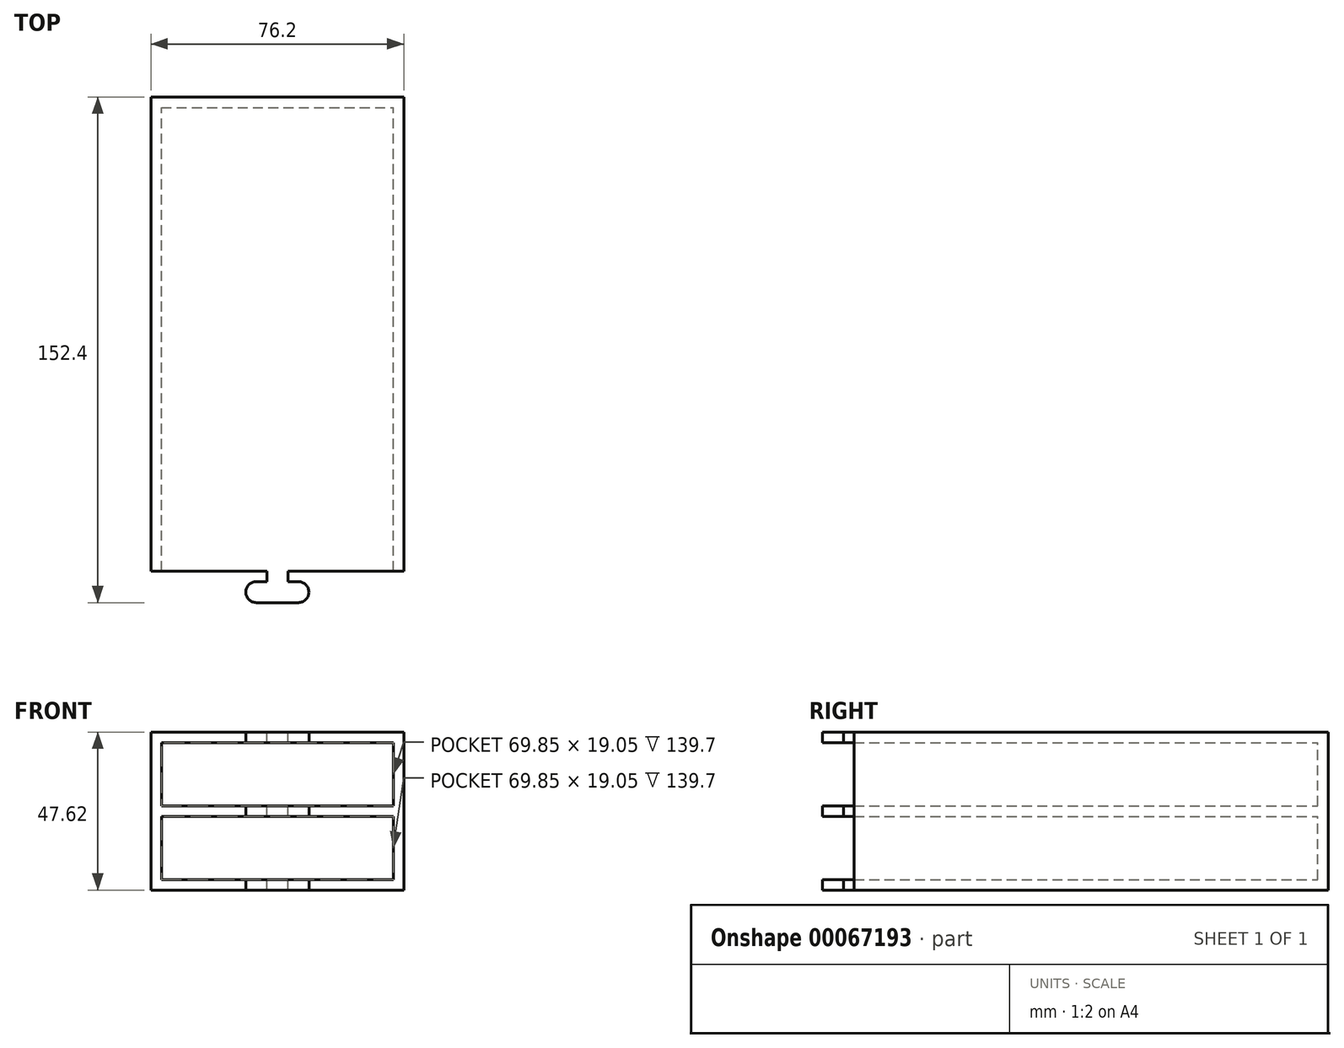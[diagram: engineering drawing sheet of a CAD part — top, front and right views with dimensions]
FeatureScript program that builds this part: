
annotation { "Feature Type Name" : "Feature", "Feature Type Description" : "" }
export const myFeature = defineFeature(function(context is Context, id is Id, definition is map)
    precondition{}
    {
        {
            var Q0;
            Q0=qCreatedBy(makeId("Front.planeOp"),FACE);
            var sketch = newSketch(context, id + "F0", { "sketchPlane" : qUnion([Q0])});
            skLineSegment(sketch, "E0.bottom", {"start": v(0, 0) * mm, "end": v(76.2, 0) * mm});
            skLineSegment(sketch, "E0.top", {"start": v(0, 47.63) * mm, "end": v(76.2, 47.63) * mm});
            skLineSegment(sketch, "E0.left", {"start": v(0, 0) * mm, "end": v(0, 47.63) * mm});
            skLineSegment(sketch, "E0.right", {"start": v(76.2, 0) * mm, "end": v(76.2, 47.63) * mm});
            skSolve(sketch);
        }
        {
            var Q0;
            Q0=makeQuery(id+"F0.imprint","IMPRINT",FACE,{"disambiguationData":[TD([[makeQuery(id+"F0.imprint","IMPRINT",EDGE,{"derivedFrom":sQuery(id+"F0.wireOp",EDGE,"E0.bottom")}),1.0]])]});
            extrude(context, id + "F1", {"entities" : qUnion([Q0]), "depth" : 3.17 * mm});
        }
        {
            var Q0;
            Q0=makeQuery(id+"F1.opExtrude","CAP_FACE",FACE,{"disambiguationData":[OSD([sQuery(id+"F0.wireOp",EDGE,"E0.bottom"),sQuery(id+"F0.wireOp",EDGE,"E0.top"),sQuery(id+"F0.wireOp",EDGE,"E0.left"),sQuery(id+"F0.wireOp",EDGE,"E0.right")])],"isStart":false});
            var sketch = newSketch(context, id + "F2", { "sketchPlane" : qUnion([Q0])});
            skLineSegment(sketch, "E1.bottom", {"start": v(3.17, 3.17) * mm, "end": v(73.03, 3.18) * mm});
            skLineSegment(sketch, "E1.top", {"start": v(3.17, 44.45) * mm, "end": v(73.03, 44.45) * mm});
            skLineSegment(sketch, "E1.left", {"start": v(3.18, 3.17) * mm, "end": v(3.18, 44.45) * mm});
            skLineSegment(sketch, "E1.right", {"start": v(73.03, 3.18) * mm, "end": v(73.03, 44.45) * mm});
            skLineSegment(sketch, "E2", {"start": v(3.17, 23.81) * mm, "end": v(73.03, 23.81) * mm});
            skLineSegment(sketch, "E3", {"start": v(73.03, 23.81) * mm, "end": v(73.03, 32.02) * mm});
            skLineSegment(sketch, "E4", {"start": v(3.18, 32.02) * mm, "end": v(3.18, 25.4) * mm});
            skLineSegment(sketch, "E5", {"start": v(3.18, 25.4) * mm, "end": v(73.03, 25.4) * mm});
            skLineSegment(sketch, "E6", {"start": v(3.17, 22.23) * mm, "end": v(73.03, 22.23) * mm});
            skSolve(sketch);
        }
        {
            var Q0;
            {var subQ0=sQuery(id+"F2.wireOp",EDGE,"E2");Q0=makeQuery(id+"F2.imprint","IMPRINT",FACE,{"disambiguationData":[TD([[makeQuery(id+"F2.imprint","IMPRINT",EDGE,{"derivedFrom":subQ0}),-1.0]])]});}
            var Q1;
            {var subQ0=sQuery(id+"F2.wireOp",EDGE,"E2");Q1=makeQuery(id+"F2.imprint","IMPRINT",FACE,{"disambiguationData":[TD([[makeQuery(id+"F2.imprint","IMPRINT",EDGE,{"derivedFrom":subQ0}),1.0]])]});}
            var Q2;
            {var subQ8=sQuery(id+"F2.wireOp",EDGE,"E1.bottom");Q2=makeQuery(id+"F2.imprint","IMPRINT",FACE,{"disambiguationData":[TD([[makeQuery(id+"F2.imprint","IMPRINT",EDGE,{"derivedFrom":subQ8}),-1.0]])]});}
            extrude(context, id + "F3", {"entities" : qUnion([Q0, Q1, Q2]), "operationType" : NewBodyOperationType.ADD, "depth" : 139.7 * mm});
        }
        {
            var Q0;
            {var subQ0=sQuery(id+"F0.wireOp",EDGE,"E0.top");Q0=makeQuery(id+"F3.boolean.opBoolean","MERGE",FACE,{"derivedFrom":[makeQuery(id+"F1.opExtrude","SWEPT_FACE",FACE,{"disambiguationData":[OSD([subQ0])]}),makeQuery(id+"F3.opExtrude","SWEPT_FACE",FACE,{"disambiguationData":[OSD([subQ0])]})]});}
            var sketch = newSketch(context, id + "F4", { "sketchPlane" : qUnion([Q0])});
            skLineSegment(sketch, "E7", {"start": v(38.1, -142.88) * mm, "end": v(38.1, -149.23) * mm});
            skLineSegment(sketch, "E8", {"start": v(38.1, -149.23) * mm, "end": v(31.75, -149.23) * mm});
            skLineSegment(sketch, "E9", {"start": v(31.75, -149.23) * mm, "end": v(44.45, -149.23) * mm});
            skCircle(sketch, "E10", {"center": v(31.75, -149.23) * mm, "radius": 3.18 * mm});
            skCircle(sketch, "E11", {"center": v(44.45, -149.23) * mm, "radius": 3.18 * mm});
            skLineSegment(sketch, "E12", {"start": v(31.75, -149.23) * mm, "end": v(31.75, -152.4) * mm});
            skLineSegment(sketch, "E13", {"start": v(31.75, -152.4) * mm, "end": v(44.45, -152.4) * mm});
            skLineSegment(sketch, "E14", {"start": v(44.45, -152.4) * mm, "end": v(44.45, -146.05) * mm});
            skLineSegment(sketch, "E15", {"start": v(44.45, -146.05) * mm, "end": v(31.75, -146.05) * mm});
            skLineSegment(sketch, "E16", {"start": v(38.1, -142.88) * mm, "end": v(34.93, -142.88) * mm});
            skLineSegment(sketch, "E17", {"start": v(34.93, -142.88) * mm, "end": v(34.93, -146.05) * mm});
            skLineSegment(sketch, "E18", {"start": v(38.1, -142.88) * mm, "end": v(41.27, -142.88) * mm});
            skLineSegment(sketch, "E19", {"start": v(41.27, -142.88) * mm, "end": v(41.27, -146.05) * mm});
            skSolve(sketch);
        }
        {
            var Q0;
            {var subQ0=sQuery(id+"F4.wireOp",EDGE,"E13");Q0=makeQuery(id+"F4.imprint","IMPRINT",FACE,{"disambiguationData":[TD([[makeQuery(id+"F4.imprint","IMPRINT",EDGE,{"derivedFrom":subQ0}),1.0]])]});}
            var Q1;
            {var subQ0=sQuery(id+"F4.wireOp",EDGE,"E12");Q1=makeQuery(id+"F4.imprint","IMPRINT",FACE,{"disambiguationData":[TD([[makeQuery(id+"F4.imprint","IMPRINT",EDGE,{"derivedFrom":subQ0}),1.0]])]});}
            var Q2;
            {var subQ0=sQuery(id+"F4.wireOp",EDGE,"E12");Q2=makeQuery(id+"F4.imprint","IMPRINT",FACE,{"disambiguationData":[TD([[makeQuery(id+"F4.imprint","IMPRINT",EDGE,{"derivedFrom":subQ0}),-1.0]])]});}
            var Q3;
            {var subQ3=sQuery(id+"F4.wireOp",EDGE,"E9");var subQ5=sQuery(id+"F4.wireOp",EDGE,"E7");var subQ6=makeQuery(id+"F4.imprint","INTERSECT",VERTEX,{"derivedFrom":[subQ5,subQ3]});Q3=makeQuery(id+"F4.imprint","IMPRINT",FACE,{"disambiguationData":[TD([[makeQuery(id+"F4.imprint","IMPRINT",EDGE,{"disambiguationData":[TD([[subQ6,1.0]])],"derivedFrom":subQ5}),-1.0]])]});}
            var Q4;
            {var subQ3=sQuery(id+"F4.wireOp",EDGE,"E9");var subQ5=sQuery(id+"F4.wireOp",EDGE,"E7");var subQ6=makeQuery(id+"F4.imprint","INTERSECT",VERTEX,{"derivedFrom":[subQ5,subQ3]});Q4=makeQuery(id+"F4.imprint","IMPRINT",FACE,{"disambiguationData":[TD([[makeQuery(id+"F4.imprint","IMPRINT",EDGE,{"disambiguationData":[TD([[subQ6,1.0]])],"derivedFrom":subQ5}),1.0]])]});}
            var Q5;
            {var subQ0=sQuery(id+"F4.wireOp",EDGE,"E14");var subQ4=makeQuery(id+"F4.imprint","INTERSECT",VERTEX,{"derivedFrom":[sQuery(id+"F4.wireOp",EDGE,"E9"),subQ0]});Q5=makeQuery(id+"F4.imprint","IMPRINT",FACE,{"disambiguationData":[TD([[makeQuery(id+"F4.imprint","IMPRINT",EDGE,{"disambiguationData":[TD([[subQ4,1.0]])],"derivedFrom":subQ0}),-1.0]])]});}
            var Q6;
            {var subQ0=sQuery(id+"F4.wireOp",EDGE,"E14");var subQ1=sQuery(id+"F4.wireOp",EDGE,"E9");var subQ2=makeQuery(id+"F4.imprint","INTERSECT",VERTEX,{"derivedFrom":[subQ1,subQ0]});Q6=makeQuery(id+"F4.imprint","IMPRINT",FACE,{"disambiguationData":[TD([[makeQuery(id+"F4.imprint","IMPRINT",EDGE,{"disambiguationData":[TD([[subQ2,1.0]])],"derivedFrom":subQ1}),1.0]])]});}
            var Q7;
            {var subQ0=sQuery(id+"F4.wireOp",EDGE,"E14");var subQ1=sQuery(id+"F4.wireOp",EDGE,"E9");var subQ2=makeQuery(id+"F4.imprint","INTERSECT",VERTEX,{"derivedFrom":[subQ1,subQ0]});Q7=makeQuery(id+"F4.imprint","IMPRINT",FACE,{"disambiguationData":[TD([[makeQuery(id+"F4.imprint","IMPRINT",EDGE,{"disambiguationData":[TD([[subQ2,1.0]])],"derivedFrom":subQ1}),-1.0]])]});}
            var Q8;
            {var subQ0=sQuery(id+"F4.wireOp",EDGE,"E18");Q8=makeQuery(id+"F4.imprint","IMPRINT",FACE,{"disambiguationData":[TD([[makeQuery(id+"F4.imprint","IMPRINT",EDGE,{"derivedFrom":subQ0}),-1.0]])]});}
            var Q9;
            {var subQ0=sQuery(id+"F4.wireOp",EDGE,"E16");Q9=makeQuery(id+"F4.imprint","IMPRINT",FACE,{"disambiguationData":[TD([[makeQuery(id+"F4.imprint","IMPRINT",EDGE,{"derivedFrom":subQ0}),-1.0]])]});}
            var Q10;
            {var subQ0=sQuery(id+"F0.wireOp",EDGE,"E0.bottom");Q10=makeQuery(id+"F3.boolean.opBoolean","MERGE",FACE,{"derivedFrom":[makeQuery(id+"F1.opExtrude","SWEPT_FACE",FACE,{"disambiguationData":[OSD([subQ0])]}),makeQuery(id+"F3.opExtrude","SWEPT_FACE",FACE,{"disambiguationData":[OSD([subQ0])]})]});}
            extrude(context, id + "F5", {"entities" : qUnion([Q0, Q1, Q2, Q3, Q4, Q5, Q6, Q7, Q8, Q9]), "operationType" : NewBodyOperationType.ADD, "endBound" : BoundingType.UP_TO_SURFACE, "oppositeDirection" : true, "endBoundEntityFace" : qUnion([Q10]), "depth" : 25.4 * mm});
        }
        {
            var Q0;
            Q0=makeQuery(id+"F3.boolean.opBoolean","SPLIT",FACE,{"disambiguationData":[TD([makeQuery(id+"F3.opExtrude","SWEPT_FACE",FACE,{"disambiguationData":[OSD([sQuery(id+"F2.wireOp",EDGE,"E1.bottom")])]})])],"derivedFrom":makeQuery(id+"F1.opExtrude","CAP_FACE",FACE,{"disambiguationData":[OSD([sQuery(id+"F0.wireOp",EDGE,"E0.bottom"),sQuery(id+"F0.wireOp",EDGE,"E0.top"),sQuery(id+"F0.wireOp",EDGE,"E0.left"),sQuery(id+"F0.wireOp",EDGE,"E0.right")])],"isStart":false})});
            var Q1;
            Q1=makeQuery(id+"F3.boolean.opBoolean","SPLIT",FACE,{"disambiguationData":[TD([makeQuery(id+"F3.opExtrude","SWEPT_FACE",FACE,{"disambiguationData":[OSD([sQuery(id+"F2.wireOp",EDGE,"E1.top")])]})])],"derivedFrom":makeQuery(id+"F1.opExtrude","CAP_FACE",FACE,{"disambiguationData":[OSD([sQuery(id+"F0.wireOp",EDGE,"E0.bottom"),sQuery(id+"F0.wireOp",EDGE,"E0.top"),sQuery(id+"F0.wireOp",EDGE,"E0.left"),sQuery(id+"F0.wireOp",EDGE,"E0.right")])],"isStart":false})});
            extrude(context, id + "F6", {"entities" : qUnion([Q0, Q1]), "operationType" : NewBodyOperationType.REMOVE, "depth" : 2540 * mm});
        }
    });
